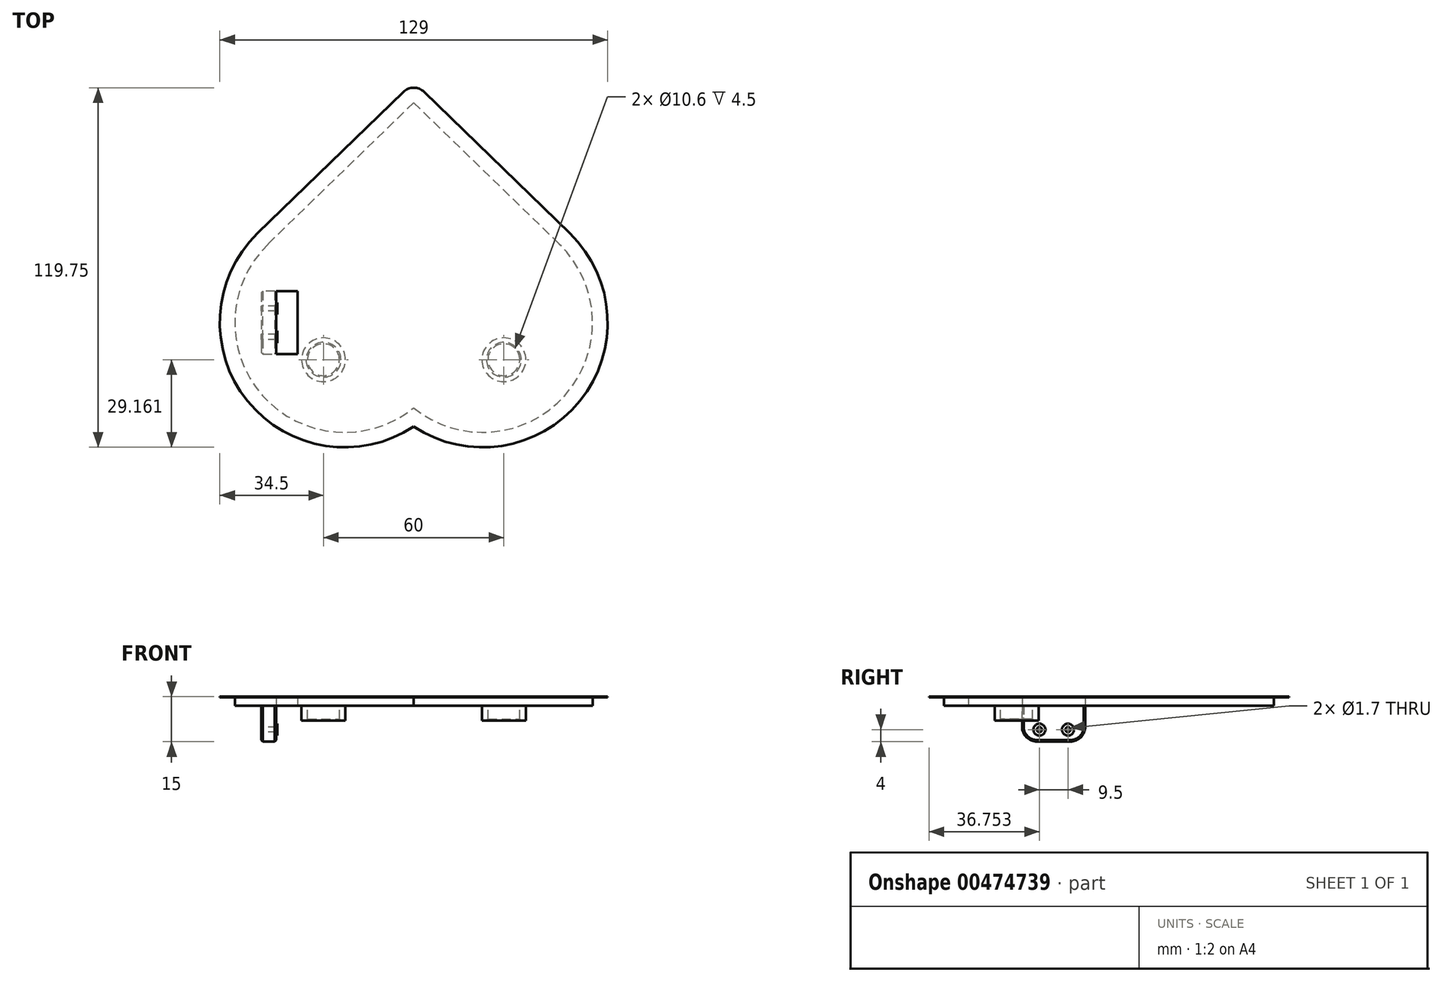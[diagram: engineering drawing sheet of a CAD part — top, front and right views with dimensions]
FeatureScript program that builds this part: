
annotation { "Feature Type Name" : "Feature", "Feature Type Description" : "" }
export const myFeature = defineFeature(function(context is Context, id is Id, definition is map)
    precondition{}
    {
        {
            var Q0;
            Q0=qCreatedBy(makeId("Top.planeOp"),FACE);
            var sketch = newSketch(context, id + "F0", { "sketchPlane" : qUnion([Q0])});
            skLineSegment(sketch, "E0", {"start": v(0, 102.93) * mm, "end": v(-48.79, 55.52) * mm, "construction": true});
            skArc(sketch, "E1", {"start": v(-48.79, 55.52) * mm, "mid": v(-50.8, 4.56) * mm, "end": v(0, 0) * mm, "construction": true});
            skArc(sketch, "E2", {"start": v(0, 0) * mm, "mid": v(50.8, 4.56) * mm, "end": v(48.79, 55.52) * mm, "construction": true});
            skLineSegment(sketch, "E3", {"start": v(0, 102.93) * mm, "end": v(48.79, 55.52) * mm, "construction": true});
            skLineSegment(sketch, "E4", {"start": v(0, 102.93) * mm, "end": v(0, 0) * mm, "construction": true});
            skLineSegment(sketch, "E5", {"start": v(-23, 28.98) * mm, "end": v(23, 28.98) * mm, "construction": true});
            skLineSegment(sketch, "E6", {"start": v(0, 102.23) * mm, "end": v(-48.44, 55.16) * mm});
            skArc(sketch, "E7", {"start": v(-48.44, 55.16) * mm, "mid": v(-50.29, 4.74) * mm, "end": v(0, 0.64) * mm});
            skArc(sketch, "E8", {"start": v(0, 0.64) * mm, "mid": v(50.29, 4.74) * mm, "end": v(48.44, 55.16) * mm});
            skLineSegment(sketch, "E9", {"start": v(0, 102.23) * mm, "end": v(48.44, 55.16) * mm});
            skSolve(sketch);
        }
        {
            var Q0;
            Q0=qSketchRegion(id+"F0",true);
            extrude(context, id + "F1", {"entities" : qUnion([Q0]), "depth" : 3 * mm, "offsetDistance" : 25 * mm});
        }
        {
            var Q0;
            Q0=makeQuery(id+"F1.opExtrude","CAP_FACE",FACE,{"disambiguationData":[OSD([sQuery(id+"F0.wireOp",EDGE,"E6"),sQuery(id+"F0.wireOp",EDGE,"E7"),sQuery(id+"F0.wireOp",EDGE,"E8"),sQuery(id+"F0.wireOp",EDGE,"E9")])],"isStart":true});
            var sketch = newSketch(context, id + "F2", { "sketchPlane" : qUnion([Q0])});
            skArc(sketch, "E10", {"start": v(0, -14.84) * mm, "mid": v(-39.88, -7.91) * mm, "end": v(-41.82, -48.35) * mm, "construction": true});
            skArc(sketch, "E11", {"start": v(41.82, -48.35) * mm, "mid": v(39.88, -7.91) * mm, "end": v(0, -14.84) * mm, "construction": true});
            skLineSegment(sketch, "E12", {"start": v(-41.82, -48.35) * mm, "end": v(0, -88.98) * mm, "construction": true});
            skLineSegment(sketch, "E13", {"start": v(0, -88.98) * mm, "end": v(41.82, -48.35) * mm, "construction": true});
            skLineSegment(sketch, "E14.bottom", {"start": v(-45.69, -18.48) * mm, "end": v(-38.69, -18.48) * mm});
            skLineSegment(sketch, "E14.top", {"start": v(-45.69, -39.48) * mm, "end": v(-38.69, -39.48) * mm});
            skLineSegment(sketch, "E14.left", {"start": v(-45.69, -18.48) * mm, "end": v(-45.69, -39.48) * mm});
            skLineSegment(sketch, "E14.right", {"start": v(-38.69, -18.48) * mm, "end": v(-38.69, -39.48) * mm});
            skSolve(sketch);
        }
        {
            var Q0;
            Q0=qSketchRegion(id+"F2",true);
            extrude(context, id + "F3", {"entities" : qUnion([Q0]), "operationType" : NewBodyOperationType.REMOVE, "endBound" : BoundingType.THROUGH_ALL, "oppositeDirection" : true, "depth" : 25 * mm, "offsetDistance" : 25 * mm});
        }
        {
            var Q0;
            Q0=makeQuery(id+"F1.opExtrude","CAP_FACE",FACE,{"disambiguationData":[OSD([sQuery(id+"F0.wireOp",EDGE,"E6"),sQuery(id+"F0.wireOp",EDGE,"E7"),sQuery(id+"F0.wireOp",EDGE,"E8"),sQuery(id+"F0.wireOp",EDGE,"E9")])],"isStart":true});
            var sketch = newSketch(context, id + "F4", { "sketchPlane" : qUnion([Q0])});
            skLineSegment(sketch, "E15", {"start": v(-45.69, -18.48) * mm, "end": v(-45.69, -39.48) * mm});
            skLineSegment(sketch, "E16", {"start": v(-45.69, -39.48) * mm, "end": v(-50.69, -39.48) * mm});
            skLineSegment(sketch, "E17", {"start": v(-50.69, -39.48) * mm, "end": v(-50.69, -18.48) * mm});
            skLineSegment(sketch, "E18", {"start": v(-50.69, -18.48) * mm, "end": v(-45.69, -18.48) * mm});
            skSolve(sketch);
        }
        {
            var Q0;
            Q0=qSketchRegion(id+"F4",true);
            extrude(context, id + "F5", {"entities" : qUnion([Q0]), "operationType" : NewBodyOperationType.ADD, "depth" : 12 * mm, "offsetDistance" : 25 * mm});
        }
        {
            var Q0;
            Q0=makeQuery(id+"F5.opExtrude","SWEPT_FACE",FACE,{"disambiguationData":[OSD([sQuery(id+"F4.wireOp",EDGE,"E17")])]});
            var sketch = newSketch(context, id + "F6", { "sketchPlane" : qUnion([Q0])});
            skLineSegment(sketch, "E19", {"start": v(-33.73, -8) * mm, "end": v(-24.23, -8) * mm, "construction": true});
            skCircle(sketch, "E20", {"center": v(-33.73, -8) * mm, "radius": 0.85 * mm});
            skCircle(sketch, "E21", {"center": v(-24.23, -8) * mm, "radius": 0.85 * mm});
            skLineSegment(sketch, "E22", {"start": v(-28.98, 0) * mm, "end": v(-28.98, -12) * mm, "construction": true});
            skSolve(sketch);
        }
        {
            var Q0;
            Q0=qSketchRegion(id+"F6",true);
            extrude(context, id + "F7", {"entities" : qUnion([Q0]), "operationType" : NewBodyOperationType.REMOVE, "endBound" : BoundingType.UP_TO_NEXT, "oppositeDirection" : true, "depth" : 25 * mm, "offsetDistance" : 25 * mm});
        }
        {
            var Q0;
            Q0=makeQuery(id+"F5.opExtrude","CAP_EDGE",EDGE,{"disambiguationData":[OSD([sQuery(id+"F4.wireOp",EDGE,"E16")])],"isStart":false});
            var Q1;
            Q1=makeQuery(id+"F5.opExtrude","CAP_EDGE",EDGE,{"disambiguationData":[OSD([sQuery(id+"F4.wireOp",EDGE,"E18")])],"isStart":false});
            fillet(context, id + "F8", {"entities" : qUnion([Q0, Q1]), "radius" : 5 * mm, "tangentPropagation" : true, "allowEdgeOverflow" : false});
        }
        {
            var Q0;
            Q0=makeQuery(id+"F5.opExtrude","CAP_EDGE",EDGE,{"disambiguationData":[OSD([sQuery(id+"F4.wireOp",EDGE,"E17")])],"isStart":false});
            var Q1;
            Q1=makeQuery(id+"F5.opExtrude","CAP_EDGE",EDGE,{"disambiguationData":[OSD([sQuery(id+"F4.wireOp",EDGE,"E15")])],"isStart":false});
            chamfer(context, id + "F9", {"entities" : qUnion([Q0, Q1]), "width" : 0.5 * mm, "tangentPropagation" : true});
        }
        {
            var Q0;
            Q0=makeQuery(id+"F5.boolean.opBoolean","MERGE",FACE,{"derivedFrom":[makeQuery(id+"F3.boolean.opBoolean","COPY",FACE,{"derivedFrom":makeQuery(id+"F3.opExtrude","SWEPT_FACE",FACE,{"disambiguationData":[OSD([sQuery(id+"F2.wireOp",EDGE,"E14.left")])]})}),makeQuery(id+"F5.opExtrude","SWEPT_FACE",FACE,{"disambiguationData":[OSD([sQuery(id+"F4.wireOp",EDGE,"E15")])]})]});
            var sketch = newSketch(context, id + "F10", { "sketchPlane" : qUnion([Q0])});
            skCircle(sketch, "E23", {"center": v(24.23, -8) * mm, "radius": 2 * mm});
            skCircle(sketch, "E24", {"center": v(33.73, -8) * mm, "radius": 2 * mm});
            skCircle(sketch, "E25", {"center": v(24.23, -8) * mm, "radius": 0.85 * mm});
            skCircle(sketch, "E26", {"center": v(33.73, -8) * mm, "radius": 0.85 * mm});
            skSolve(sketch);
        }
        {
            var Q0;
            Q0=qSketchRegion(id+"F10",true);
            extrude(context, id + "F11", {"entities" : qUnion([Q0]), "operationType" : NewBodyOperationType.ADD, "depth" : 0.3 * mm, "offsetDistance" : 25 * mm});
        }
        {
            var Q0;
            Q0=makeQuery(id+"F1.opExtrude","CAP_FACE",FACE,{"disambiguationData":[OSD([sQuery(id+"F0.wireOp",EDGE,"E6"),sQuery(id+"F0.wireOp",EDGE,"E7"),sQuery(id+"F0.wireOp",EDGE,"E8"),sQuery(id+"F0.wireOp",EDGE,"E9")])],"isStart":true});
            var sketch = newSketch(context, id + "F12", { "sketchPlane" : qUnion([Q0])});
            skCircle(sketch, "E27", {"center": v(-30, -16.64) * mm, "radius": 7.3 * mm});
            skCircle(sketch, "E28", {"center": v(-30, -16.64) * mm, "radius": 5.3 * mm});
            skCircle(sketch, "E29", {"center": v(30, -16.64) * mm, "radius": 7.3 * mm});
            skCircle(sketch, "E30", {"center": v(30, -16.64) * mm, "radius": 5.3 * mm});
            skLineSegment(sketch, "E31", {"start": v(0, -0.64) * mm, "end": v(0, -102.23) * mm, "construction": true});
            skLineSegment(sketch, "E32", {"start": v(-30, -16.64) * mm, "end": v(30, -16.64) * mm, "construction": true});
            skSolve(sketch);
        }
        {
            var Q0;
            Q0=qSketchRegion(id+"F12",true);
            extrude(context, id + "F13", {"entities" : qUnion([Q0]), "operationType" : NewBodyOperationType.ADD, "depth" : 5 * mm, "offsetDistance" : 25 * mm});
        }
        {
            var Q0;
            Q0=makeQuery(id+"F13.opExtrude","CAP_EDGE",EDGE,{"disambiguationData":[OSD([sQuery(id+"F12.wireOp",EDGE,"E28")])],"isStart":false});
            var Q1;
            Q1=makeQuery(id+"F13.opExtrude","CAP_EDGE",EDGE,{"disambiguationData":[OSD([sQuery(id+"F12.wireOp",EDGE,"E30")])],"isStart":false});
            chamfer(context, id + "F14", {"entities" : qUnion([Q0, Q1]), "width" : 0.5 * mm, "tangentPropagation" : true});
        }
        {
            var Q0;
            Q0=makeQuery(id+"F1.opExtrude","CAP_FACE",FACE,{"disambiguationData":[OSD([sQuery(id+"F0.wireOp",EDGE,"E6"),sQuery(id+"F0.wireOp",EDGE,"E7"),sQuery(id+"F0.wireOp",EDGE,"E8"),sQuery(id+"F0.wireOp",EDGE,"E9")])],"isStart":false});
            var sketch = newSketch(context, id + "F15", { "sketchPlane" : qUnion([Q0])});
            skLineSegment(sketch, "E33", {"start": v(0, 102.23) * mm, "end": v(-48.44, 55.16) * mm});
            skLineSegment(sketch, "E34", {"start": v(0, 102.23) * mm, "end": v(48.44, 55.16) * mm});
            skArc(sketch, "E35", {"start": v(-48.44, 55.16) * mm, "mid": v(-50.29, 4.74) * mm, "end": v(0, 0.64) * mm});
            skArc(sketch, "E36", {"start": v(0, 0.64) * mm, "mid": v(50.29, 4.74) * mm, "end": v(48.44, 55.16) * mm});
            skLineSegment(sketch, "E37", {"start": v(-51.92, 58.74) * mm, "end": v(-3.48, 105.82) * mm});
            skLineSegment(sketch, "E38", {"start": v(51.92, 58.74) * mm, "end": v(3.48, 105.82) * mm});
            skArc(sketch, "E39", {"start": v(3.48, 105.82) * mm, "mid": v(0, 107.23) * mm, "end": v(-3.48, 105.82) * mm});
            skArc(sketch, "E40", {"start": v(-51.92, 58.74) * mm, "mid": v(-55.29, 2.91) * mm, "end": v(0, -5.56) * mm});
            skArc(sketch, "E41", {"start": v(0, -5.56) * mm, "mid": v(55.29, 2.91) * mm, "end": v(51.92, 58.74) * mm});
            skSolve(sketch);
        }
        {
            var Q0;
            Q0 = qSketchRegion(id + "F15", true);
            extrude(context, id + "F16", {"entities" : qUnion([Q0]), "operationType" : NewBodyOperationType.ADD, "oppositeDirection" : true, "depth" : 0.2 * mm, "offsetDistance" : 25 * mm});
        }
    });
